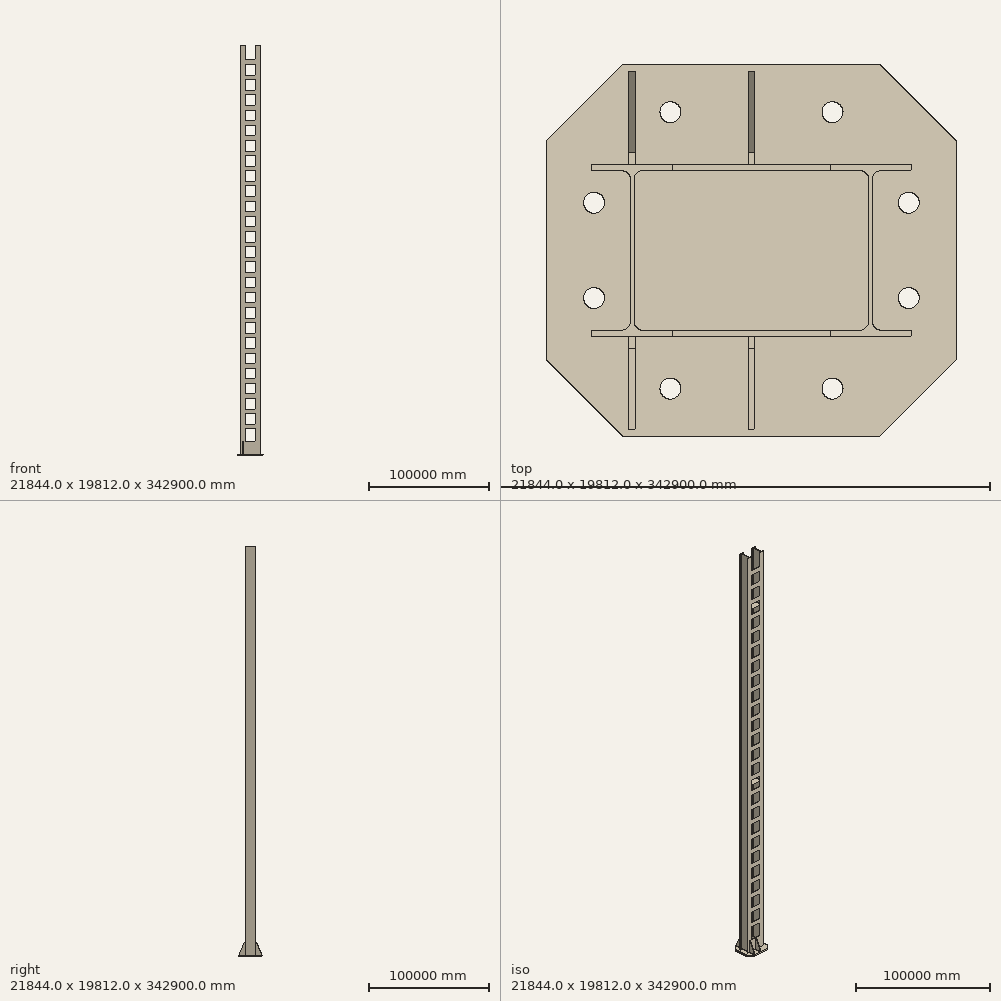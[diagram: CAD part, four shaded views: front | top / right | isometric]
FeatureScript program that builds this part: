
annotation { "Feature Type Name" : "Feature", "Feature Type Description" : "" }
export const myFeature = defineFeature(function(context is Context, id is Id, definition is map)
    precondition{}
    {
        {
            var Q0;
            Q0=qCreatedBy(makeId("Top.planeOp"),FACE);
            var sketch = newSketch(context, id + "F0", { "sketchPlane" : qUnion([Q0])});
            skLineSegment(sketch, "E0", {"start": v(-8509, 4572) * mm, "end": v(8509, 4572) * mm});
            skLineSegment(sketch, "E1", {"start": v(8509, 4572) * mm, "end": v(8509, 4249.42) * mm});
            skLineSegment(sketch, "E2", {"start": v(8509, 4249.42) * mm, "end": v(6908.8, 4249.42) * mm});
            skLineSegment(sketch, "E3", {"start": v(6451.6, 3792.22) * mm, "end": v(6451.6, -3792.22) * mm});
            skLineSegment(sketch, "E4", {"start": v(6908.8, -4249.42) * mm, "end": v(8509, -4249.42) * mm});
            skLineSegment(sketch, "E5", {"start": v(8509, -4249.42) * mm, "end": v(8509, -4572) * mm});
            skLineSegment(sketch, "E6", {"start": v(8509, -4572) * mm, "end": v(-8509, -4572) * mm});
            skLineSegment(sketch, "E7", {"start": v(-8509, -4572) * mm, "end": v(-8509, -4249.42) * mm});
            skLineSegment(sketch, "E8", {"start": v(-8509, -4249.42) * mm, "end": v(-6908.8, -4249.42) * mm});
            skLineSegment(sketch, "E9", {"start": v(-6451.6, -3792.22) * mm, "end": v(-6451.6, 3792.22) * mm});
            skLineSegment(sketch, "E10", {"start": v(-6908.8, 4249.42) * mm, "end": v(-8509, 4249.42) * mm});
            skLineSegment(sketch, "E11", {"start": v(-8509, 4249.42) * mm, "end": v(-8509, 4572) * mm});
            skPoint(sketch, "E12.visualSharp", {"position": v(-6451.6, 4249.42) * mm});
            skArc(sketch, "E12.filletArc", {"start": v(-6451.6, 3792.22) * mm, "mid": v(-6585.51, 4115.5) * mm, "end": v(-6908.8, 4249.42) * mm});
            skPoint(sketch, "E13.visualSharp", {"position": v(6451.6, 4249.42) * mm});
            skArc(sketch, "E13.filletArc", {"start": v(6908.8, 4249.42) * mm, "mid": v(6585.51, 4115.5) * mm, "end": v(6451.6, 3792.22) * mm});
            skPoint(sketch, "E14.visualSharp", {"position": v(6451.6, -4249.42) * mm});
            skArc(sketch, "E14.filletArc", {"start": v(6451.6, -3792.22) * mm, "mid": v(6585.51, -4115.5) * mm, "end": v(6908.8, -4249.42) * mm});
            skPoint(sketch, "E15.visualSharp", {"position": v(-6451.6, -4249.42) * mm});
            skArc(sketch, "E15.filletArc", {"start": v(-6908.8, -4249.42) * mm, "mid": v(-6585.51, -4115.5) * mm, "end": v(-6451.6, -3792.22) * mm});
            skSolve(sketch);
        }
        {
            var Q0;
            Q0 = qSketchRegion(id + "F0", true);
            extrude(context, id + "F1", {"entities" : qUnion([Q0]), "depth" : 342900 * mm});
        }
        {
            var Q0;
            Q0=makeQuery(id+"F1.opExtrude","CAP_FACE",FACE,{"disambiguationData":[OSD([sQuery(id+"F0.wireOp",EDGE,"E0"),sQuery(id+"F0.wireOp",EDGE,"E1"),sQuery(id+"F0.wireOp",EDGE,"E2"),sQuery(id+"F0.wireOp",EDGE,"E3"),sQuery(id+"F0.wireOp",EDGE,"E4"),sQuery(id+"F0.wireOp",EDGE,"E5"),sQuery(id+"F0.wireOp",EDGE,"E6"),sQuery(id+"F0.wireOp",EDGE,"E7"),sQuery(id+"F0.wireOp",EDGE,"E8"),sQuery(id+"F0.wireOp",EDGE,"E9"),sQuery(id+"F0.wireOp",EDGE,"E10"),sQuery(id+"F0.wireOp",EDGE,"E11"),sQuery(id+"F0.wireOp",EDGE,"E12.filletArc"),sQuery(id+"F0.wireOp",EDGE,"E13.filletArc"),sQuery(id+"F0.wireOp",EDGE,"E14.filletArc"),sQuery(id+"F0.wireOp",EDGE,"E15.filletArc")])],"isStart":true});
            var sketch = newSketch(context, id + "F2", { "sketchPlane" : qUnion([Q0])});
            skLineSegment(sketch, "E16.bottom", {"start": v(-5791.2, 4249.42) * mm, "end": v(5791.2, 4249.42) * mm});
            skLineSegment(sketch, "E16.top", {"start": v(-5791.2, -4249.42) * mm, "end": v(5791.2, -4249.42) * mm});
            skLineSegment(sketch, "E16.left", {"start": v(-6248.4, 3792.22) * mm, "end": v(-6248.4, -3792.22) * mm});
            skLineSegment(sketch, "E16.right", {"start": v(6248.4, 3792.22) * mm, "end": v(6248.4, -3792.22) * mm});
            skPoint(sketch, "E17.visualSharp", {"position": v(-6248.4, 4249.42) * mm});
            skArc(sketch, "E17.filletArc", {"start": v(-5791.2, 4249.42) * mm, "mid": v(-6114.49, 4115.5) * mm, "end": v(-6248.4, 3792.22) * mm});
            skPoint(sketch, "E18.visualSharp", {"position": v(6248.4, 4249.42) * mm});
            skArc(sketch, "E18.filletArc", {"start": v(6248.4, 3792.22) * mm, "mid": v(6114.49, 4115.5) * mm, "end": v(5791.2, 4249.42) * mm});
            skPoint(sketch, "E19.visualSharp", {"position": v(6248.4, -4249.42) * mm});
            skArc(sketch, "E19.filletArc", {"start": v(5791.2, -4249.42) * mm, "mid": v(6114.49, -4115.5) * mm, "end": v(6248.4, -3792.22) * mm});
            skPoint(sketch, "E20.visualSharp", {"position": v(-6248.4, -4249.42) * mm});
            skArc(sketch, "E20.filletArc", {"start": v(-6248.4, -3792.22) * mm, "mid": v(-6114.49, -4115.5) * mm, "end": v(-5791.2, -4249.42) * mm});
            skLineSegment(sketch, "E21", {"start": v(-6913.3, 0) * mm, "end": v(6813.76, 0) * mm, "construction": true});
            skLineSegment(sketch, "E22", {"start": v(0, 5029.13) * mm, "end": v(0, -5231.93) * mm, "construction": true});
            skSolve(sketch);
        }
        {
            var Q0;
            Q0 = qSketchRegion(id + "F2", true);
            extrude(context, id + "F3", {"entities" : qUnion([Q0]), "operationType" : NewBodyOperationType.REMOVE, "endBound" : BoundingType.THROUGH_ALL, "oppositeDirection" : true, "depth" : 25.4 * mm});
        }
        {
            var Q0;
            Q0=makeQuery(id+"F1.opExtrude","SWEPT_FACE",FACE,{"disambiguationData":[OSD([sQuery(id+"F0.wireOp",EDGE,"E6")])]});
            var sketch = newSketch(context, id + "F4", { "sketchPlane" : qUnion([Q0])});
            skLineSegment(sketch, "E23.bottom", {"start": v(-4191, 34925) * mm, "end": v(4191, 34925) * mm});
            skLineSegment(sketch, "E23.top", {"start": v(-4191, 26035) * mm, "end": v(4191, 26035) * mm});
            skLineSegment(sketch, "E23.left", {"start": v(-4191, 34925) * mm, "end": v(-4191, 26035) * mm});
            skLineSegment(sketch, "E23.right", {"start": v(4191, 34925) * mm, "end": v(4191, 26035) * mm});
            skLineSegment(sketch, "E24", {"start": v(0, -2627.58) * mm, "end": v(0, 406140.36) * mm, "construction": true});
            skLineSegment(sketch, "E25.0.1.0", {"start": v(-4191, 47625) * mm, "end": v(4191, 47625) * mm});
            skLineSegment(sketch, "E25.0.1.1", {"start": v(-4191, 38735) * mm, "end": v(4191, 38735) * mm});
            skLineSegment(sketch, "E25.0.1.2", {"start": v(-4191, 47625) * mm, "end": v(-4191, 38735) * mm});
            skLineSegment(sketch, "E25.0.1.3", {"start": v(4191, 47625) * mm, "end": v(4191, 38735) * mm});
            skLineSegment(sketch, "E25.0.2.0", {"start": v(-4191, 60325) * mm, "end": v(4191, 60325) * mm});
            skLineSegment(sketch, "E25.0.2.1", {"start": v(-4191, 51435) * mm, "end": v(4191, 51435) * mm});
            skLineSegment(sketch, "E25.0.2.2", {"start": v(-4191, 60325) * mm, "end": v(-4191, 51435) * mm});
            skLineSegment(sketch, "E25.0.2.3", {"start": v(4191, 60325) * mm, "end": v(4191, 51435) * mm});
            skLineSegment(sketch, "E25.0.3.0", {"start": v(-4191, 73025) * mm, "end": v(4191, 73025) * mm});
            skLineSegment(sketch, "E25.0.3.1", {"start": v(-4191, 64135) * mm, "end": v(4191, 64135) * mm});
            skLineSegment(sketch, "E25.0.3.2", {"start": v(-4191, 73025) * mm, "end": v(-4191, 64135) * mm});
            skLineSegment(sketch, "E25.0.3.3", {"start": v(4191, 73025) * mm, "end": v(4191, 64135) * mm});
            skLineSegment(sketch, "E25.0.4.0", {"start": v(-4191, 85725) * mm, "end": v(4191, 85725) * mm});
            skLineSegment(sketch, "E25.0.4.1", {"start": v(-4191, 76835) * mm, "end": v(4191, 76835) * mm});
            skLineSegment(sketch, "E25.0.4.2", {"start": v(-4191, 85725) * mm, "end": v(-4191, 76835) * mm});
            skLineSegment(sketch, "E25.0.4.3", {"start": v(4191, 85725) * mm, "end": v(4191, 76835) * mm});
            skLineSegment(sketch, "E25.0.5.0", {"start": v(-4191, 98425) * mm, "end": v(4191, 98425) * mm});
            skLineSegment(sketch, "E25.0.5.1", {"start": v(-4191, 89535) * mm, "end": v(4191, 89535) * mm});
            skLineSegment(sketch, "E25.0.5.2", {"start": v(-4191, 98425) * mm, "end": v(-4191, 89535) * mm});
            skLineSegment(sketch, "E25.0.5.3", {"start": v(4191, 98425) * mm, "end": v(4191, 89535) * mm});
            skLineSegment(sketch, "E25.0.6.0", {"start": v(-4191, 111125) * mm, "end": v(4191, 111125) * mm});
            skLineSegment(sketch, "E25.0.6.1", {"start": v(-4191, 102235) * mm, "end": v(4191, 102235) * mm});
            skLineSegment(sketch, "E25.0.6.2", {"start": v(-4191, 111125) * mm, "end": v(-4191, 102235) * mm});
            skLineSegment(sketch, "E25.0.6.3", {"start": v(4191, 111125) * mm, "end": v(4191, 102235) * mm});
            skLineSegment(sketch, "E25.0.7.0", {"start": v(-4191, 123825) * mm, "end": v(4191, 123825) * mm});
            skLineSegment(sketch, "E25.0.7.1", {"start": v(-4191, 114935) * mm, "end": v(4191, 114935) * mm});
            skLineSegment(sketch, "E25.0.7.2", {"start": v(-4191, 123825) * mm, "end": v(-4191, 114935) * mm});
            skLineSegment(sketch, "E25.0.7.3", {"start": v(4191, 123825) * mm, "end": v(4191, 114935) * mm});
            skLineSegment(sketch, "E25.0.8.0", {"start": v(-4191, 136525) * mm, "end": v(4191, 136525) * mm});
            skLineSegment(sketch, "E25.0.8.1", {"start": v(-4191, 127635) * mm, "end": v(4191, 127635) * mm});
            skLineSegment(sketch, "E25.0.8.2", {"start": v(-4191, 136525) * mm, "end": v(-4191, 127635) * mm});
            skLineSegment(sketch, "E25.0.8.3", {"start": v(4191, 136525) * mm, "end": v(4191, 127635) * mm});
            skLineSegment(sketch, "E25.0.9.0", {"start": v(-4191, 149225) * mm, "end": v(4191, 149225) * mm});
            skLineSegment(sketch, "E25.0.9.1", {"start": v(-4191, 140335) * mm, "end": v(4191, 140335) * mm});
            skLineSegment(sketch, "E25.0.9.2", {"start": v(-4191, 149225) * mm, "end": v(-4191, 140335) * mm});
            skLineSegment(sketch, "E25.0.9.3", {"start": v(4191, 149225) * mm, "end": v(4191, 140335) * mm});
            skLineSegment(sketch, "E25.0.10.0", {"start": v(-4191, 161925) * mm, "end": v(4191, 161925) * mm});
            skLineSegment(sketch, "E25.0.10.1", {"start": v(-4191, 153035) * mm, "end": v(4191, 153035) * mm});
            skLineSegment(sketch, "E25.0.10.2", {"start": v(-4191, 161925) * mm, "end": v(-4191, 153035) * mm});
            skLineSegment(sketch, "E25.0.10.3", {"start": v(4191, 161925) * mm, "end": v(4191, 153035) * mm});
            skLineSegment(sketch, "E25.0.11.0", {"start": v(-4191, 174625) * mm, "end": v(4191, 174625) * mm});
            skLineSegment(sketch, "E25.0.11.1", {"start": v(-4191, 165735) * mm, "end": v(4191, 165735) * mm});
            skLineSegment(sketch, "E25.0.11.2", {"start": v(-4191, 174625) * mm, "end": v(-4191, 165735) * mm});
            skLineSegment(sketch, "E25.0.11.3", {"start": v(4191, 174625) * mm, "end": v(4191, 165735) * mm});
            skLineSegment(sketch, "E25.0.12.0", {"start": v(-4191, 187325) * mm, "end": v(4191, 187325) * mm});
            skLineSegment(sketch, "E25.0.12.1", {"start": v(-4191, 178435) * mm, "end": v(4191, 178435) * mm});
            skLineSegment(sketch, "E25.0.12.2", {"start": v(-4191, 187325) * mm, "end": v(-4191, 178435) * mm});
            skLineSegment(sketch, "E25.0.12.3", {"start": v(4191, 187325) * mm, "end": v(4191, 178435) * mm});
            skLineSegment(sketch, "E25.0.13.0", {"start": v(-4191, 200025) * mm, "end": v(4191, 200025) * mm});
            skLineSegment(sketch, "E25.0.13.1", {"start": v(-4191, 191135) * mm, "end": v(4191, 191135) * mm});
            skLineSegment(sketch, "E25.0.13.2", {"start": v(-4191, 200025) * mm, "end": v(-4191, 191135) * mm});
            skLineSegment(sketch, "E25.0.13.3", {"start": v(4191, 200025) * mm, "end": v(4191, 191135) * mm});
            skLineSegment(sketch, "E25.0.14.0", {"start": v(-4191, 212725) * mm, "end": v(4191, 212725) * mm});
            skLineSegment(sketch, "E25.0.14.1", {"start": v(-4191, 203835) * mm, "end": v(4191, 203835) * mm});
            skLineSegment(sketch, "E25.0.14.2", {"start": v(-4191, 212725) * mm, "end": v(-4191, 203835) * mm});
            skLineSegment(sketch, "E25.0.14.3", {"start": v(4191, 212725) * mm, "end": v(4191, 203835) * mm});
            skLineSegment(sketch, "E25.0.15.0", {"start": v(-4191, 225425) * mm, "end": v(4191, 225425) * mm});
            skLineSegment(sketch, "E25.0.15.1", {"start": v(-4191, 216535) * mm, "end": v(4191, 216535) * mm});
            skLineSegment(sketch, "E25.0.15.2", {"start": v(-4191, 225425) * mm, "end": v(-4191, 216535) * mm});
            skLineSegment(sketch, "E25.0.15.3", {"start": v(4191, 225425) * mm, "end": v(4191, 216535) * mm});
            skLineSegment(sketch, "E25.0.16.0", {"start": v(-4191, 238125) * mm, "end": v(4191, 238125) * mm});
            skLineSegment(sketch, "E25.0.16.1", {"start": v(-4191, 229235) * mm, "end": v(4191, 229235) * mm});
            skLineSegment(sketch, "E25.0.16.2", {"start": v(-4191, 238125) * mm, "end": v(-4191, 229235) * mm});
            skLineSegment(sketch, "E25.0.16.3", {"start": v(4191, 238125) * mm, "end": v(4191, 229235) * mm});
            skLineSegment(sketch, "E25.0.17.0", {"start": v(-4191, 250825) * mm, "end": v(4191, 250825) * mm});
            skLineSegment(sketch, "E25.0.17.1", {"start": v(-4191, 241935) * mm, "end": v(4191, 241935) * mm});
            skLineSegment(sketch, "E25.0.17.2", {"start": v(-4191, 250825) * mm, "end": v(-4191, 241935) * mm});
            skLineSegment(sketch, "E25.0.17.3", {"start": v(4191, 250825) * mm, "end": v(4191, 241935) * mm});
            skLineSegment(sketch, "E25.0.18.0", {"start": v(-4191, 263525) * mm, "end": v(4191, 263525) * mm});
            skLineSegment(sketch, "E25.0.18.1", {"start": v(-4191, 254635) * mm, "end": v(4191, 254635) * mm});
            skLineSegment(sketch, "E25.0.18.2", {"start": v(-4191, 263525) * mm, "end": v(-4191, 254635) * mm});
            skLineSegment(sketch, "E25.0.18.3", {"start": v(4191, 263525) * mm, "end": v(4191, 254635) * mm});
            skLineSegment(sketch, "E25.0.19.0", {"start": v(-4191, 276225) * mm, "end": v(4191, 276225) * mm});
            skLineSegment(sketch, "E25.0.19.1", {"start": v(-4191, 267335) * mm, "end": v(4191, 267335) * mm});
            skLineSegment(sketch, "E25.0.19.2", {"start": v(-4191, 276225) * mm, "end": v(-4191, 267335) * mm});
            skLineSegment(sketch, "E25.0.19.3", {"start": v(4191, 276225) * mm, "end": v(4191, 267335) * mm});
            skLineSegment(sketch, "E25.0.20.0", {"start": v(-4191, 288925) * mm, "end": v(4191, 288925) * mm});
            skLineSegment(sketch, "E25.0.20.1", {"start": v(-4191, 280035) * mm, "end": v(4191, 280035) * mm});
            skLineSegment(sketch, "E25.0.20.2", {"start": v(-4191, 288925) * mm, "end": v(-4191, 280035) * mm});
            skLineSegment(sketch, "E25.0.20.3", {"start": v(4191, 288925) * mm, "end": v(4191, 280035) * mm});
            skLineSegment(sketch, "E25.0.21.0", {"start": v(-4191, 301625) * mm, "end": v(4191, 301625) * mm});
            skLineSegment(sketch, "E25.0.21.1", {"start": v(-4191, 292735) * mm, "end": v(4191, 292735) * mm});
            skLineSegment(sketch, "E25.0.21.2", {"start": v(-4191, 301625) * mm, "end": v(-4191, 292735) * mm});
            skLineSegment(sketch, "E25.0.21.3", {"start": v(4191, 301625) * mm, "end": v(4191, 292735) * mm});
            skLineSegment(sketch, "E25.0.22.0", {"start": v(-4191, 314325) * mm, "end": v(4191, 314325) * mm});
            skLineSegment(sketch, "E25.0.22.1", {"start": v(-4191, 305435) * mm, "end": v(4191, 305435) * mm});
            skLineSegment(sketch, "E25.0.22.2", {"start": v(-4191, 314325) * mm, "end": v(-4191, 305435) * mm});
            skLineSegment(sketch, "E25.0.22.3", {"start": v(4191, 314325) * mm, "end": v(4191, 305435) * mm});
            skLineSegment(sketch, "E25.0.23.0", {"start": v(-4191, 327025) * mm, "end": v(4191, 327025) * mm});
            skLineSegment(sketch, "E25.0.23.1", {"start": v(-4191, 318135) * mm, "end": v(4191, 318135) * mm});
            skLineSegment(sketch, "E25.0.23.2", {"start": v(-4191, 327025) * mm, "end": v(-4191, 318135) * mm});
            skLineSegment(sketch, "E25.0.23.3", {"start": v(4191, 327025) * mm, "end": v(4191, 318135) * mm});
            skLineSegment(sketch, "E25.1.1.0", {"start": v(-4191, 47625) * mm, "end": v(4191, 47625) * mm});
            skLineSegment(sketch, "E25.1.1.1", {"start": v(-4191, 38735) * mm, "end": v(4191, 38735) * mm});
            skLineSegment(sketch, "E25.1.1.2", {"start": v(-4191, 47625) * mm, "end": v(-4191, 38735) * mm});
            skLineSegment(sketch, "E25.1.1.3", {"start": v(4191, 47625) * mm, "end": v(4191, 38735) * mm});
            skLineSegment(sketch, "E25.1.2.0", {"start": v(-4191, 60325) * mm, "end": v(4191, 60325) * mm});
            skLineSegment(sketch, "E25.1.2.1", {"start": v(-4191, 51435) * mm, "end": v(4191, 51435) * mm});
            skLineSegment(sketch, "E25.1.2.2", {"start": v(-4191, 60325) * mm, "end": v(-4191, 51435) * mm});
            skLineSegment(sketch, "E25.1.2.3", {"start": v(4191, 60325) * mm, "end": v(4191, 51435) * mm});
            skLineSegment(sketch, "E25.1.3.0", {"start": v(-4191, 73025) * mm, "end": v(4191, 73025) * mm});
            skLineSegment(sketch, "E25.1.3.1", {"start": v(-4191, 64135) * mm, "end": v(4191, 64135) * mm});
            skLineSegment(sketch, "E25.1.3.2", {"start": v(-4191, 73025) * mm, "end": v(-4191, 64135) * mm});
            skLineSegment(sketch, "E25.1.3.3", {"start": v(4191, 73025) * mm, "end": v(4191, 64135) * mm});
            skLineSegment(sketch, "E25.1.4.0", {"start": v(-4191, 85725) * mm, "end": v(4191, 85725) * mm});
            skLineSegment(sketch, "E25.1.4.1", {"start": v(-4191, 76835) * mm, "end": v(4191, 76835) * mm});
            skLineSegment(sketch, "E25.1.4.2", {"start": v(-4191, 85725) * mm, "end": v(-4191, 76835) * mm});
            skLineSegment(sketch, "E25.1.4.3", {"start": v(4191, 85725) * mm, "end": v(4191, 76835) * mm});
            skLineSegment(sketch, "E25.1.5.0", {"start": v(-4191, 98425) * mm, "end": v(4191, 98425) * mm});
            skLineSegment(sketch, "E25.1.5.1", {"start": v(-4191, 89535) * mm, "end": v(4191, 89535) * mm});
            skLineSegment(sketch, "E25.1.5.2", {"start": v(-4191, 98425) * mm, "end": v(-4191, 89535) * mm});
            skLineSegment(sketch, "E25.1.5.3", {"start": v(4191, 98425) * mm, "end": v(4191, 89535) * mm});
            skLineSegment(sketch, "E25.1.6.0", {"start": v(-4191, 111125) * mm, "end": v(4191, 111125) * mm});
            skLineSegment(sketch, "E25.1.6.1", {"start": v(-4191, 102235) * mm, "end": v(4191, 102235) * mm});
            skLineSegment(sketch, "E25.1.6.2", {"start": v(-4191, 111125) * mm, "end": v(-4191, 102235) * mm});
            skLineSegment(sketch, "E25.1.6.3", {"start": v(4191, 111125) * mm, "end": v(4191, 102235) * mm});
            skLineSegment(sketch, "E25.1.7.0", {"start": v(-4191, 123825) * mm, "end": v(4191, 123825) * mm});
            skLineSegment(sketch, "E25.1.7.1", {"start": v(-4191, 114935) * mm, "end": v(4191, 114935) * mm});
            skLineSegment(sketch, "E25.1.7.2", {"start": v(-4191, 123825) * mm, "end": v(-4191, 114935) * mm});
            skLineSegment(sketch, "E25.1.7.3", {"start": v(4191, 123825) * mm, "end": v(4191, 114935) * mm});
            skLineSegment(sketch, "E25.1.8.0", {"start": v(-4191, 136525) * mm, "end": v(4191, 136525) * mm});
            skLineSegment(sketch, "E25.1.8.1", {"start": v(-4191, 127635) * mm, "end": v(4191, 127635) * mm});
            skLineSegment(sketch, "E25.1.8.2", {"start": v(-4191, 136525) * mm, "end": v(-4191, 127635) * mm});
            skLineSegment(sketch, "E25.1.8.3", {"start": v(4191, 136525) * mm, "end": v(4191, 127635) * mm});
            skLineSegment(sketch, "E25.1.9.0", {"start": v(-4191, 149225) * mm, "end": v(4191, 149225) * mm});
            skLineSegment(sketch, "E25.1.9.1", {"start": v(-4191, 140335) * mm, "end": v(4191, 140335) * mm});
            skLineSegment(sketch, "E25.1.9.2", {"start": v(-4191, 149225) * mm, "end": v(-4191, 140335) * mm});
            skLineSegment(sketch, "E25.1.9.3", {"start": v(4191, 149225) * mm, "end": v(4191, 140335) * mm});
            skLineSegment(sketch, "E25.1.10.0", {"start": v(-4191, 161925) * mm, "end": v(4191, 161925) * mm});
            skLineSegment(sketch, "E25.1.10.1", {"start": v(-4191, 153035) * mm, "end": v(4191, 153035) * mm});
            skLineSegment(sketch, "E25.1.10.2", {"start": v(-4191, 161925) * mm, "end": v(-4191, 153035) * mm});
            skLineSegment(sketch, "E25.1.10.3", {"start": v(4191, 161925) * mm, "end": v(4191, 153035) * mm});
            skLineSegment(sketch, "E25.1.11.0", {"start": v(-4191, 174625) * mm, "end": v(4191, 174625) * mm});
            skLineSegment(sketch, "E25.1.11.1", {"start": v(-4191, 165735) * mm, "end": v(4191, 165735) * mm});
            skLineSegment(sketch, "E25.1.11.2", {"start": v(-4191, 174625) * mm, "end": v(-4191, 165735) * mm});
            skLineSegment(sketch, "E25.1.11.3", {"start": v(4191, 174625) * mm, "end": v(4191, 165735) * mm});
            skLineSegment(sketch, "E25.1.12.0", {"start": v(-4191, 187325) * mm, "end": v(4191, 187325) * mm});
            skLineSegment(sketch, "E25.1.12.1", {"start": v(-4191, 178435) * mm, "end": v(4191, 178435) * mm});
            skLineSegment(sketch, "E25.1.12.2", {"start": v(-4191, 187325) * mm, "end": v(-4191, 178435) * mm});
            skLineSegment(sketch, "E25.1.12.3", {"start": v(4191, 187325) * mm, "end": v(4191, 178435) * mm});
            skLineSegment(sketch, "E25.1.13.0", {"start": v(-4191, 200025) * mm, "end": v(4191, 200025) * mm});
            skLineSegment(sketch, "E25.1.13.1", {"start": v(-4191, 191135) * mm, "end": v(4191, 191135) * mm});
            skLineSegment(sketch, "E25.1.13.2", {"start": v(-4191, 200025) * mm, "end": v(-4191, 191135) * mm});
            skLineSegment(sketch, "E25.1.13.3", {"start": v(4191, 200025) * mm, "end": v(4191, 191135) * mm});
            skLineSegment(sketch, "E25.1.14.0", {"start": v(-4191, 212725) * mm, "end": v(4191, 212725) * mm});
            skLineSegment(sketch, "E25.1.14.1", {"start": v(-4191, 203835) * mm, "end": v(4191, 203835) * mm});
            skLineSegment(sketch, "E25.1.14.2", {"start": v(-4191, 212725) * mm, "end": v(-4191, 203835) * mm});
            skLineSegment(sketch, "E25.1.14.3", {"start": v(4191, 212725) * mm, "end": v(4191, 203835) * mm});
            skLineSegment(sketch, "E25.1.15.0", {"start": v(-4191, 225425) * mm, "end": v(4191, 225425) * mm});
            skLineSegment(sketch, "E25.1.15.1", {"start": v(-4191, 216535) * mm, "end": v(4191, 216535) * mm});
            skLineSegment(sketch, "E25.1.15.2", {"start": v(-4191, 225425) * mm, "end": v(-4191, 216535) * mm});
            skLineSegment(sketch, "E25.1.15.3", {"start": v(4191, 225425) * mm, "end": v(4191, 216535) * mm});
            skLineSegment(sketch, "E25.1.16.0", {"start": v(-4191, 238125) * mm, "end": v(4191, 238125) * mm});
            skLineSegment(sketch, "E25.1.16.1", {"start": v(-4191, 229235) * mm, "end": v(4191, 229235) * mm});
            skLineSegment(sketch, "E25.1.16.2", {"start": v(-4191, 238125) * mm, "end": v(-4191, 229235) * mm});
            skLineSegment(sketch, "E25.1.16.3", {"start": v(4191, 238125) * mm, "end": v(4191, 229235) * mm});
            skLineSegment(sketch, "E25.1.17.0", {"start": v(-4191, 250825) * mm, "end": v(4191, 250825) * mm});
            skLineSegment(sketch, "E25.1.17.1", {"start": v(-4191, 241935) * mm, "end": v(4191, 241935) * mm});
            skLineSegment(sketch, "E25.1.17.2", {"start": v(-4191, 250825) * mm, "end": v(-4191, 241935) * mm});
            skLineSegment(sketch, "E25.1.17.3", {"start": v(4191, 250825) * mm, "end": v(4191, 241935) * mm});
            skLineSegment(sketch, "E25.1.18.0", {"start": v(-4191, 263525) * mm, "end": v(4191, 263525) * mm});
            skLineSegment(sketch, "E25.1.18.1", {"start": v(-4191, 254635) * mm, "end": v(4191, 254635) * mm});
            skLineSegment(sketch, "E25.1.18.2", {"start": v(-4191, 263525) * mm, "end": v(-4191, 254635) * mm});
            skLineSegment(sketch, "E25.1.18.3", {"start": v(4191, 263525) * mm, "end": v(4191, 254635) * mm});
            skLineSegment(sketch, "E25.1.19.0", {"start": v(-4191, 276225) * mm, "end": v(4191, 276225) * mm});
            skLineSegment(sketch, "E25.1.19.1", {"start": v(-4191, 267335) * mm, "end": v(4191, 267335) * mm});
            skLineSegment(sketch, "E25.1.19.2", {"start": v(-4191, 276225) * mm, "end": v(-4191, 267335) * mm});
            skLineSegment(sketch, "E25.1.19.3", {"start": v(4191, 276225) * mm, "end": v(4191, 267335) * mm});
            skLineSegment(sketch, "E25.1.20.0", {"start": v(-4191, 288925) * mm, "end": v(4191, 288925) * mm});
            skLineSegment(sketch, "E25.1.20.1", {"start": v(-4191, 280035) * mm, "end": v(4191, 280035) * mm});
            skLineSegment(sketch, "E25.1.20.2", {"start": v(-4191, 288925) * mm, "end": v(-4191, 280035) * mm});
            skLineSegment(sketch, "E25.1.20.3", {"start": v(4191, 288925) * mm, "end": v(4191, 280035) * mm});
            skLineSegment(sketch, "E25.1.21.0", {"start": v(-4191, 301625) * mm, "end": v(4191, 301625) * mm});
            skLineSegment(sketch, "E25.1.21.1", {"start": v(-4191, 292735) * mm, "end": v(4191, 292735) * mm});
            skLineSegment(sketch, "E25.1.21.2", {"start": v(-4191, 301625) * mm, "end": v(-4191, 292735) * mm});
            skLineSegment(sketch, "E25.1.21.3", {"start": v(4191, 301625) * mm, "end": v(4191, 292735) * mm});
            skLineSegment(sketch, "E25.1.22.0", {"start": v(-4191, 314325) * mm, "end": v(4191, 314325) * mm});
            skLineSegment(sketch, "E25.1.22.1", {"start": v(-4191, 305435) * mm, "end": v(4191, 305435) * mm});
            skLineSegment(sketch, "E25.1.22.2", {"start": v(-4191, 314325) * mm, "end": v(-4191, 305435) * mm});
            skLineSegment(sketch, "E25.1.22.3", {"start": v(4191, 314325) * mm, "end": v(4191, 305435) * mm});
            skLineSegment(sketch, "E25.1.23.0", {"start": v(-4191, 327025) * mm, "end": v(4191, 327025) * mm});
            skLineSegment(sketch, "E25.1.23.1", {"start": v(-4191, 318135) * mm, "end": v(4191, 318135) * mm});
            skLineSegment(sketch, "E25.1.23.2", {"start": v(-4191, 327025) * mm, "end": v(-4191, 318135) * mm});
            skLineSegment(sketch, "E25.1.23.3", {"start": v(4191, 327025) * mm, "end": v(4191, 318135) * mm});
            skLineSegment(sketch, "E25.2.1.0", {"start": v(-4191, 47625) * mm, "end": v(4191, 47625) * mm});
            skLineSegment(sketch, "E25.2.1.1", {"start": v(-4191, 38735) * mm, "end": v(4191, 38735) * mm});
            skLineSegment(sketch, "E25.2.1.2", {"start": v(-4191, 47625) * mm, "end": v(-4191, 38735) * mm});
            skLineSegment(sketch, "E25.2.1.3", {"start": v(4191, 47625) * mm, "end": v(4191, 38735) * mm});
            skLineSegment(sketch, "E25.2.2.0", {"start": v(-4191, 60325) * mm, "end": v(4191, 60325) * mm});
            skLineSegment(sketch, "E25.2.2.1", {"start": v(-4191, 51435) * mm, "end": v(4191, 51435) * mm});
            skLineSegment(sketch, "E25.2.2.2", {"start": v(-4191, 60325) * mm, "end": v(-4191, 51435) * mm});
            skLineSegment(sketch, "E25.2.2.3", {"start": v(4191, 60325) * mm, "end": v(4191, 51435) * mm});
            skLineSegment(sketch, "E25.2.3.0", {"start": v(-4191, 73025) * mm, "end": v(4191, 73025) * mm});
            skLineSegment(sketch, "E25.2.3.1", {"start": v(-4191, 64135) * mm, "end": v(4191, 64135) * mm});
            skLineSegment(sketch, "E25.2.3.2", {"start": v(-4191, 73025) * mm, "end": v(-4191, 64135) * mm});
            skLineSegment(sketch, "E25.2.3.3", {"start": v(4191, 73025) * mm, "end": v(4191, 64135) * mm});
            skLineSegment(sketch, "E25.2.4.0", {"start": v(-4191, 85725) * mm, "end": v(4191, 85725) * mm});
            skLineSegment(sketch, "E25.2.4.1", {"start": v(-4191, 76835) * mm, "end": v(4191, 76835) * mm});
            skLineSegment(sketch, "E25.2.4.2", {"start": v(-4191, 85725) * mm, "end": v(-4191, 76835) * mm});
            skLineSegment(sketch, "E25.2.4.3", {"start": v(4191, 85725) * mm, "end": v(4191, 76835) * mm});
            skLineSegment(sketch, "E25.2.5.0", {"start": v(-4191, 98425) * mm, "end": v(4191, 98425) * mm});
            skLineSegment(sketch, "E25.2.5.1", {"start": v(-4191, 89535) * mm, "end": v(4191, 89535) * mm});
            skLineSegment(sketch, "E25.2.5.2", {"start": v(-4191, 98425) * mm, "end": v(-4191, 89535) * mm});
            skLineSegment(sketch, "E25.2.5.3", {"start": v(4191, 98425) * mm, "end": v(4191, 89535) * mm});
            skLineSegment(sketch, "E25.2.6.0", {"start": v(-4191, 111125) * mm, "end": v(4191, 111125) * mm});
            skLineSegment(sketch, "E25.2.6.1", {"start": v(-4191, 102235) * mm, "end": v(4191, 102235) * mm});
            skLineSegment(sketch, "E25.2.6.2", {"start": v(-4191, 111125) * mm, "end": v(-4191, 102235) * mm});
            skLineSegment(sketch, "E25.2.6.3", {"start": v(4191, 111125) * mm, "end": v(4191, 102235) * mm});
            skLineSegment(sketch, "E25.2.7.0", {"start": v(-4191, 123825) * mm, "end": v(4191, 123825) * mm});
            skLineSegment(sketch, "E25.2.7.1", {"start": v(-4191, 114935) * mm, "end": v(4191, 114935) * mm});
            skLineSegment(sketch, "E25.2.7.2", {"start": v(-4191, 123825) * mm, "end": v(-4191, 114935) * mm});
            skLineSegment(sketch, "E25.2.7.3", {"start": v(4191, 123825) * mm, "end": v(4191, 114935) * mm});
            skLineSegment(sketch, "E25.2.8.0", {"start": v(-4191, 136525) * mm, "end": v(4191, 136525) * mm});
            skLineSegment(sketch, "E25.2.8.1", {"start": v(-4191, 127635) * mm, "end": v(4191, 127635) * mm});
            skLineSegment(sketch, "E25.2.8.2", {"start": v(-4191, 136525) * mm, "end": v(-4191, 127635) * mm});
            skLineSegment(sketch, "E25.2.8.3", {"start": v(4191, 136525) * mm, "end": v(4191, 127635) * mm});
            skLineSegment(sketch, "E25.2.9.0", {"start": v(-4191, 149225) * mm, "end": v(4191, 149225) * mm});
            skLineSegment(sketch, "E25.2.9.1", {"start": v(-4191, 140335) * mm, "end": v(4191, 140335) * mm});
            skLineSegment(sketch, "E25.2.9.2", {"start": v(-4191, 149225) * mm, "end": v(-4191, 140335) * mm});
            skLineSegment(sketch, "E25.2.9.3", {"start": v(4191, 149225) * mm, "end": v(4191, 140335) * mm});
            skLineSegment(sketch, "E25.2.10.0", {"start": v(-4191, 161925) * mm, "end": v(4191, 161925) * mm});
            skLineSegment(sketch, "E25.2.10.1", {"start": v(-4191, 153035) * mm, "end": v(4191, 153035) * mm});
            skLineSegment(sketch, "E25.2.10.2", {"start": v(-4191, 161925) * mm, "end": v(-4191, 153035) * mm});
            skLineSegment(sketch, "E25.2.10.3", {"start": v(4191, 161925) * mm, "end": v(4191, 153035) * mm});
            skLineSegment(sketch, "E25.2.11.0", {"start": v(-4191, 174625) * mm, "end": v(4191, 174625) * mm});
            skLineSegment(sketch, "E25.2.11.1", {"start": v(-4191, 165735) * mm, "end": v(4191, 165735) * mm});
            skLineSegment(sketch, "E25.2.11.2", {"start": v(-4191, 174625) * mm, "end": v(-4191, 165735) * mm});
            skLineSegment(sketch, "E25.2.11.3", {"start": v(4191, 174625) * mm, "end": v(4191, 165735) * mm});
            skLineSegment(sketch, "E25.2.12.0", {"start": v(-4191, 187325) * mm, "end": v(4191, 187325) * mm});
            skLineSegment(sketch, "E25.2.12.1", {"start": v(-4191, 178435) * mm, "end": v(4191, 178435) * mm});
            skLineSegment(sketch, "E25.2.12.2", {"start": v(-4191, 187325) * mm, "end": v(-4191, 178435) * mm});
            skLineSegment(sketch, "E25.2.12.3", {"start": v(4191, 187325) * mm, "end": v(4191, 178435) * mm});
            skLineSegment(sketch, "E25.2.13.0", {"start": v(-4191, 200025) * mm, "end": v(4191, 200025) * mm});
            skLineSegment(sketch, "E25.2.13.1", {"start": v(-4191, 191135) * mm, "end": v(4191, 191135) * mm});
            skLineSegment(sketch, "E25.2.13.2", {"start": v(-4191, 200025) * mm, "end": v(-4191, 191135) * mm});
            skLineSegment(sketch, "E25.2.13.3", {"start": v(4191, 200025) * mm, "end": v(4191, 191135) * mm});
            skLineSegment(sketch, "E25.2.14.0", {"start": v(-4191, 212725) * mm, "end": v(4191, 212725) * mm});
            skLineSegment(sketch, "E25.2.14.1", {"start": v(-4191, 203835) * mm, "end": v(4191, 203835) * mm});
            skLineSegment(sketch, "E25.2.14.2", {"start": v(-4191, 212725) * mm, "end": v(-4191, 203835) * mm});
            skLineSegment(sketch, "E25.2.14.3", {"start": v(4191, 212725) * mm, "end": v(4191, 203835) * mm});
            skLineSegment(sketch, "E25.2.15.0", {"start": v(-4191, 225425) * mm, "end": v(4191, 225425) * mm});
            skLineSegment(sketch, "E25.2.15.1", {"start": v(-4191, 216535) * mm, "end": v(4191, 216535) * mm});
            skLineSegment(sketch, "E25.2.15.2", {"start": v(-4191, 225425) * mm, "end": v(-4191, 216535) * mm});
            skLineSegment(sketch, "E25.2.15.3", {"start": v(4191, 225425) * mm, "end": v(4191, 216535) * mm});
            skLineSegment(sketch, "E25.2.16.0", {"start": v(-4191, 238125) * mm, "end": v(4191, 238125) * mm});
            skLineSegment(sketch, "E25.2.16.1", {"start": v(-4191, 229235) * mm, "end": v(4191, 229235) * mm});
            skLineSegment(sketch, "E25.2.16.2", {"start": v(-4191, 238125) * mm, "end": v(-4191, 229235) * mm});
            skLineSegment(sketch, "E25.2.16.3", {"start": v(4191, 238125) * mm, "end": v(4191, 229235) * mm});
            skLineSegment(sketch, "E25.2.17.0", {"start": v(-4191, 250825) * mm, "end": v(4191, 250825) * mm});
            skLineSegment(sketch, "E25.2.17.1", {"start": v(-4191, 241935) * mm, "end": v(4191, 241935) * mm});
            skLineSegment(sketch, "E25.2.17.2", {"start": v(-4191, 250825) * mm, "end": v(-4191, 241935) * mm});
            skLineSegment(sketch, "E25.2.17.3", {"start": v(4191, 250825) * mm, "end": v(4191, 241935) * mm});
            skLineSegment(sketch, "E25.2.18.0", {"start": v(-4191, 263525) * mm, "end": v(4191, 263525) * mm});
            skLineSegment(sketch, "E25.2.18.1", {"start": v(-4191, 254635) * mm, "end": v(4191, 254635) * mm});
            skLineSegment(sketch, "E25.2.18.2", {"start": v(-4191, 263525) * mm, "end": v(-4191, 254635) * mm});
            skLineSegment(sketch, "E25.2.18.3", {"start": v(4191, 263525) * mm, "end": v(4191, 254635) * mm});
            skLineSegment(sketch, "E25.2.19.0", {"start": v(-4191, 276225) * mm, "end": v(4191, 276225) * mm});
            skLineSegment(sketch, "E25.2.19.1", {"start": v(-4191, 267335) * mm, "end": v(4191, 267335) * mm});
            skLineSegment(sketch, "E25.2.19.2", {"start": v(-4191, 276225) * mm, "end": v(-4191, 267335) * mm});
            skLineSegment(sketch, "E25.2.19.3", {"start": v(4191, 276225) * mm, "end": v(4191, 267335) * mm});
            skLineSegment(sketch, "E25.2.20.0", {"start": v(-4191, 288925) * mm, "end": v(4191, 288925) * mm});
            skLineSegment(sketch, "E25.2.20.1", {"start": v(-4191, 280035) * mm, "end": v(4191, 280035) * mm});
            skLineSegment(sketch, "E25.2.20.2", {"start": v(-4191, 288925) * mm, "end": v(-4191, 280035) * mm});
            skLineSegment(sketch, "E25.2.20.3", {"start": v(4191, 288925) * mm, "end": v(4191, 280035) * mm});
            skLineSegment(sketch, "E25.2.21.0", {"start": v(-4191, 301625) * mm, "end": v(4191, 301625) * mm});
            skLineSegment(sketch, "E25.2.21.1", {"start": v(-4191, 292735) * mm, "end": v(4191, 292735) * mm});
            skLineSegment(sketch, "E25.2.21.2", {"start": v(-4191, 301625) * mm, "end": v(-4191, 292735) * mm});
            skLineSegment(sketch, "E25.2.21.3", {"start": v(4191, 301625) * mm, "end": v(4191, 292735) * mm});
            skLineSegment(sketch, "E25.2.22.0", {"start": v(-4191, 314325) * mm, "end": v(4191, 314325) * mm});
            skLineSegment(sketch, "E25.2.22.1", {"start": v(-4191, 305435) * mm, "end": v(4191, 305435) * mm});
            skLineSegment(sketch, "E25.2.22.2", {"start": v(-4191, 314325) * mm, "end": v(-4191, 305435) * mm});
            skLineSegment(sketch, "E25.2.22.3", {"start": v(4191, 314325) * mm, "end": v(4191, 305435) * mm});
            skLineSegment(sketch, "E25.2.23.0", {"start": v(-4191, 327025) * mm, "end": v(4191, 327025) * mm});
            skLineSegment(sketch, "E25.2.23.1", {"start": v(-4191, 318135) * mm, "end": v(4191, 318135) * mm});
            skLineSegment(sketch, "E25.2.23.2", {"start": v(-4191, 327025) * mm, "end": v(-4191, 318135) * mm});
            skLineSegment(sketch, "E25.2.23.3", {"start": v(4191, 327025) * mm, "end": v(4191, 318135) * mm});
            skLineSegment(sketch, "E25.direction1", {"start": v(-4191, 26035) * mm, "end": v(-4191, 26035) * mm});
            skLineSegment(sketch, "E25.direction2", {"start": v(-4191, 26035) * mm, "end": v(-4191, 38735) * mm, "construction": true});
            skLineSegment(sketch, "E26.bottom", {"start": v(-4191, 342900) * mm, "end": v(4191, 342900) * mm});
            skLineSegment(sketch, "E26.top", {"start": v(-4191, 330835) * mm, "end": v(4191, 330835) * mm});
            skLineSegment(sketch, "E26.left", {"start": v(-4191, 342900) * mm, "end": v(-4191, 330835) * mm});
            skLineSegment(sketch, "E26.right", {"start": v(4191, 342900) * mm, "end": v(4191, 330835) * mm});
            skLineSegment(sketch, "E27.bottom", {"start": v(-4191, 22225) * mm, "end": v(4191, 22225) * mm});
            skLineSegment(sketch, "E27.top", {"start": v(-4191, 11303) * mm, "end": v(4191, 11303) * mm});
            skLineSegment(sketch, "E27.left", {"start": v(-4191, 22225) * mm, "end": v(-4191, 11303) * mm});
            skLineSegment(sketch, "E27.right", {"start": v(4191, 22225) * mm, "end": v(4191, 11303) * mm});
            skSolve(sketch);
        }
        {
            var Q0;
            Q0 = qSketchRegion(id + "F4", true);
            extrude(context, id + "F5", {"entities" : qUnion([Q0]), "operationType" : NewBodyOperationType.REMOVE, "endBound" : BoundingType.THROUGH_ALL, "oppositeDirection" : true, "depth" : 25.4 * mm});
        }
        {
            var Q0;
            Q0=qCreatedBy(makeId("Top.planeOp"),FACE);
            cPlane(context, id + "F6", {"entities" : qUnion([Q0]), "cplaneType" : CPlaneType.OFFSET, "offset" : 144780 * mm, "width" : 152.4 * mm, "height" : 152.4 * mm});
        }
        {
            var Q0;
            Q0=qCreatedBy(id+"F6.planeOp",FACE);
            var sketch = newSketch(context, id + "F7", { "sketchPlane" : qUnion([Q0])});
            skLineSegment(sketch, "E28", {"start": v(0, 5038.5) * mm, "end": v(0, -5387.54) * mm, "construction": true});
            skLineSegment(sketch, "E29", {"start": v(-6816.57, 0) * mm, "end": v(7079.48, 0) * mm, "construction": true});
            skLineSegment(sketch, "E30.bottom", {"start": v(-5791.2, 4249.42) * mm, "end": v(5791.2, 4249.42) * mm});
            skLineSegment(sketch, "E30.top", {"start": v(-5791.2, -4249.42) * mm, "end": v(5791.2, -4249.42) * mm});
            skLineSegment(sketch, "E30.left", {"start": v(-6248.4, 3792.22) * mm, "end": v(-6248.4, -3792.22) * mm});
            skLineSegment(sketch, "E30.right", {"start": v(6248.4, 3792.22) * mm, "end": v(6248.4, -3792.22) * mm});
            skPoint(sketch, "E31.visualSharp", {"position": v(-6248.4, 4249.42) * mm});
            skArc(sketch, "E31.filletArc", {"start": v(-5791.2, 4249.42) * mm, "mid": v(-6114.49, 4115.5) * mm, "end": v(-6248.4, 3792.22) * mm});
            skPoint(sketch, "E32.visualSharp", {"position": v(6248.4, 4249.42) * mm});
            skArc(sketch, "E32.filletArc", {"start": v(6248.4, 3792.22) * mm, "mid": v(6114.49, 4115.5) * mm, "end": v(5791.2, 4249.42) * mm});
            skPoint(sketch, "E33.visualSharp", {"position": v(6248.4, -4249.42) * mm});
            skArc(sketch, "E33.filletArc", {"start": v(5791.2, -4249.42) * mm, "mid": v(6114.49, -4115.5) * mm, "end": v(6248.4, -3792.22) * mm});
            skPoint(sketch, "E34.visualSharp", {"position": v(-6248.4, -4249.42) * mm});
            skArc(sketch, "E34.filletArc", {"start": v(-6248.4, -3792.22) * mm, "mid": v(-6114.49, -4115.5) * mm, "end": v(-5791.2, -4249.42) * mm});
            skSolve(sketch);
        }
        {
            var Q0;
            Q0 = qSketchRegion(id + "F7", true);
            extrude(context, id + "F8", {"entities" : qUnion([Q0]), "operationType" : NewBodyOperationType.ADD, "endBound" : BoundingType.SYMMETRIC, "depth" : 152.4 * mm});
        }
        {
            var Q0;
            Q0=qCreatedBy(makeId("Top.planeOp"),FACE);
            cPlane(context, id + "F9", {"entities" : qUnion([Q0]), "cplaneType" : CPlaneType.OFFSET, "offset" : 297180 * mm, "width" : 152.4 * mm, "height" : 152.4 * mm});
        }
        {
            var Q0;
            Q0=qCreatedBy(id+"F9.planeOp",FACE);
            var sketch = newSketch(context, id + "F10", { "sketchPlane" : qUnion([Q0])});
            skLineSegment(sketch, "E35.bottom", {"start": v(-5791.2, 4249.42) * mm, "end": v(5791.2, 4249.42) * mm});
            skLineSegment(sketch, "E35.top", {"start": v(-5791.2, -4249.42) * mm, "end": v(5791.2, -4249.42) * mm});
            skLineSegment(sketch, "E35.left", {"start": v(-6248.4, 3792.22) * mm, "end": v(-6248.4, -3792.22) * mm});
            skLineSegment(sketch, "E35.right", {"start": v(6248.4, 3792.22) * mm, "end": v(6248.4, -3792.22) * mm});
            skLineSegment(sketch, "E36", {"start": v(-6862.25, 0) * mm, "end": v(7060.04, 0) * mm, "construction": true});
            skLineSegment(sketch, "E37", {"start": v(0, 5227.84) * mm, "end": v(0, -5440.7) * mm, "construction": true});
            skPoint(sketch, "E38.visualSharp", {"position": v(-6248.4, 4249.42) * mm});
            skArc(sketch, "E38.filletArc", {"start": v(-5791.2, 4249.42) * mm, "mid": v(-6114.49, 4115.5) * mm, "end": v(-6248.4, 3792.22) * mm});
            skPoint(sketch, "E39.visualSharp", {"position": v(6248.4, 4249.42) * mm});
            skArc(sketch, "E39.filletArc", {"start": v(6248.4, 3792.22) * mm, "mid": v(6114.49, 4115.5) * mm, "end": v(5791.2, 4249.42) * mm});
            skPoint(sketch, "E40.visualSharp", {"position": v(6248.4, -4249.42) * mm});
            skArc(sketch, "E40.filletArc", {"start": v(5791.2, -4249.42) * mm, "mid": v(6114.49, -4115.5) * mm, "end": v(6248.4, -3792.22) * mm});
            skPoint(sketch, "E41.visualSharp", {"position": v(-6248.4, -4249.42) * mm});
            skArc(sketch, "E41.filletArc", {"start": v(-6248.4, -3792.22) * mm, "mid": v(-6114.49, -4115.5) * mm, "end": v(-5791.2, -4249.42) * mm});
            skSolve(sketch);
        }
        {
            var Q0;
            Q0 = qSketchRegion(id + "F10", true);
            extrude(context, id + "F11", {"entities" : qUnion([Q0]), "operationType" : NewBodyOperationType.ADD, "endBound" : BoundingType.SYMMETRIC, "depth" : 152.4 * mm});
        }
        {
            var Q0;
            Q0=qCreatedBy(makeId("Right.planeOp"),FACE);
            var sketch = newSketch(context, id + "F12", { "sketchPlane" : qUnion([Q0])});
            skLineSegment(sketch, "E42", {"start": v(-9525, 0) * mm, "end": v(-9525, 1778) * mm});
            skLineSegment(sketch, "E43", {"start": v(-9525, 1778) * mm, "end": v(-5207, 11303) * mm});
            skLineSegment(sketch, "E44", {"start": v(-5207, 11303) * mm, "end": v(5207, 11303) * mm});
            skLineSegment(sketch, "E45", {"start": v(5207, 11303) * mm, "end": v(9525, 1778) * mm});
            skLineSegment(sketch, "E46", {"start": v(9525, 1778) * mm, "end": v(9525, 0) * mm});
            skLineSegment(sketch, "E47", {"start": v(9525, 0) * mm, "end": v(-9525, 0) * mm});
            skLineSegment(sketch, "E48", {"start": v(0, -2307.15) * mm, "end": v(0, 14569.66) * mm, "construction": true});
            skSolve(sketch);
        }
        {
            var Q0;
            Q0 = qSketchRegion(id + "F12", true);
            extrude(context, id + "F13", {"entities" : qUnion([Q0]), "operationType" : NewBodyOperationType.ADD, "endBound" : BoundingType.SYMMETRIC, "depth" : 304.8 * mm});
        }
        {
            var Q0;
            Q0=qCreatedBy(makeId("Right.planeOp"),FACE);
            cPlane(context, id + "F14", {"entities" : qUnion([Q0]), "cplaneType" : CPlaneType.OFFSET, "offset" : 6350 * mm, "width" : 152.4 * mm, "height" : 152.4 * mm});
        }
        {
            var Q0;
            Q0=qCreatedBy(makeId("Right.planeOp"),FACE);
            cPlane(context, id + "F15", {"entities" : qUnion([Q0]), "cplaneType" : CPlaneType.OFFSET, "offset" : 6350 * mm, "oppositeDirection" : true, "width" : 152.4 * mm, "height" : 152.4 * mm});
        }
        {
            var Q0;
            Q0=qCreatedBy(id+"F15.planeOp",FACE);
            var sketch = newSketch(context, id + "F16", { "sketchPlane" : qUnion([Q0])});
            skLineSegment(sketch, "E49", {"start": v(4572, 0) * mm, "end": v(4572, 11303) * mm});
            skLineSegment(sketch, "E50", {"start": v(4572, 11303) * mm, "end": v(5207, 11303) * mm});
            skLineSegment(sketch, "E51", {"start": v(5207, 11303) * mm, "end": v(9525, 1778) * mm});
            skLineSegment(sketch, "E52", {"start": v(9525, 1778) * mm, "end": v(9525, 0) * mm});
            skLineSegment(sketch, "E53", {"start": v(9525, 0) * mm, "end": v(4572, 0) * mm});
            skLineSegment(sketch, "E54", {"start": v(0, -2703.1) * mm, "end": v(0, 13730.2) * mm, "construction": true});
            skLineSegment(sketch, "E55.MirrorCS", {"start": v(-4572, 11303) * mm, "end": v(-5207, 11303) * mm});
            skLineSegment(sketch, "E56.MirrorCS", {"start": v(-5207, 11303) * mm, "end": v(-9525, 1778) * mm});
            skLineSegment(sketch, "E57.MirrorCS", {"start": v(-4572, 0) * mm, "end": v(-4572, 11303) * mm});
            skLineSegment(sketch, "E58.MirrorCS", {"start": v(-9525, 1778) * mm, "end": v(-9525, 0) * mm});
            skLineSegment(sketch, "E59.MirrorCS", {"start": v(-9525, 0) * mm, "end": v(-4572, 0) * mm});
            skSolve(sketch);
        }
        {
            var Q0;
            Q0 = qSketchRegion(id + "F16", true);
            extrude(context, id + "F17", {"entities" : qUnion([Q0]), "operationType" : NewBodyOperationType.ADD, "endBound" : BoundingType.SYMMETRIC, "depth" : 355.6 * mm});
        }
        {
            var Q0;
            Q0=qCreatedBy(makeId("Top.planeOp"),FACE);
            var sketch = newSketch(context, id + "F18", { "sketchPlane" : qUnion([Q0])});
            skLineSegment(sketch, "E60", {"start": v(-10922, -5842) * mm, "end": v(-10922, 5842) * mm});
            skLineSegment(sketch, "E61", {"start": v(-10922, 5842) * mm, "end": v(-6858, 9906) * mm});
            skLineSegment(sketch, "E62", {"start": v(-6858, 9906) * mm, "end": v(6858, 9906) * mm});
            skLineSegment(sketch, "E63", {"start": v(6858, 9906) * mm, "end": v(10922, 5842) * mm});
            skLineSegment(sketch, "E64", {"start": v(10922, 5842) * mm, "end": v(10922, -5842) * mm});
            skLineSegment(sketch, "E65", {"start": v(10922, -5842) * mm, "end": v(6858, -9906) * mm});
            skLineSegment(sketch, "E66", {"start": v(6858, -9906) * mm, "end": v(-6858, -9906) * mm});
            skLineSegment(sketch, "E67", {"start": v(-6858, -9906) * mm, "end": v(-10922, -5842) * mm});
            skLineSegment(sketch, "E68", {"start": v(0, 11047.18) * mm, "end": v(0, -11914.8) * mm, "construction": true});
            skLineSegment(sketch, "E69", {"start": v(-11304.08, 0) * mm, "end": v(12211.2, 0) * mm, "construction": true});
            skCircle(sketch, "E70", {"center": v(4318, 7366) * mm, "radius": 558.8 * mm});
            skCircle(sketch, "E71", {"center": v(8382, 2540) * mm, "radius": 558.8 * mm});
            skCircle(sketch, "E72.MirrorC", {"center": v(4318, -7366) * mm, "radius": 558.8 * mm});
            skCircle(sketch, "E73.MirrorC", {"center": v(8382, -2540) * mm, "radius": 558.8 * mm});
            skCircle(sketch, "E74.MirrorC", {"center": v(-4318, -7366) * mm, "radius": 558.8 * mm});
            skCircle(sketch, "E75.MirrorC", {"center": v(-4318, 7366) * mm, "radius": 558.8 * mm});
            skCircle(sketch, "E76.MirrorC", {"center": v(-8382, 2540) * mm, "radius": 558.8 * mm});
            skCircle(sketch, "E77.MirrorC", {"center": v(-8382, -2540) * mm, "radius": 558.8 * mm});
            skSolve(sketch);
        }
        {
            var Q0;
            Q0 = qSketchRegion(id + "F18", true);
            extrude(context, id + "F19", {"entities" : qUnion([Q0]), "operationType" : NewBodyOperationType.ADD, "depth" : 1143 * mm});
        }
    });
